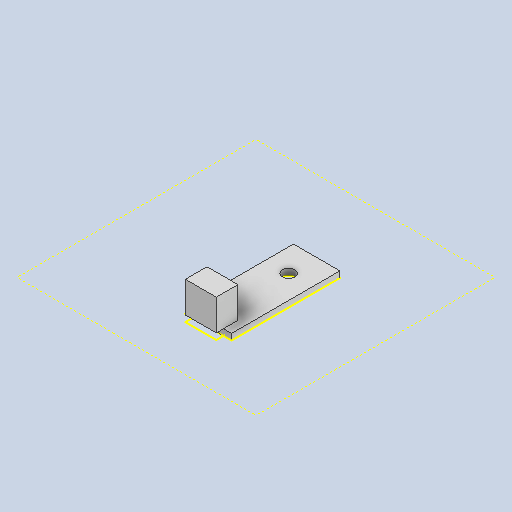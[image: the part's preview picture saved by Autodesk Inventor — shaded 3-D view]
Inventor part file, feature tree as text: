
AUTODESK INVENTOR PART (.ipt)
format: ipt  version: 2025.1 (Build 291241000, 241)  size: 94,208 bytes
history: native  units: in
note: dims shown in document units (in); Inventor stores cm internally (conversion verified against a paired STEP export)
features: other x3, sketch x1
ambient origin geometry x8: Origin, YZ Plane, XZ Plane, XY Plane, X Axis, Y Axis, Z Axis, Center Point
bodies: Solid1 (feature_tree)
feature tree (4):
  other  "Sensor ky-037.ipt"
  other  "Solid1::Sensor ky-037.ipt"
  other  "TaggingFeature1"
  sketch  "Sketch1"  dims[d0=0.3937in]
